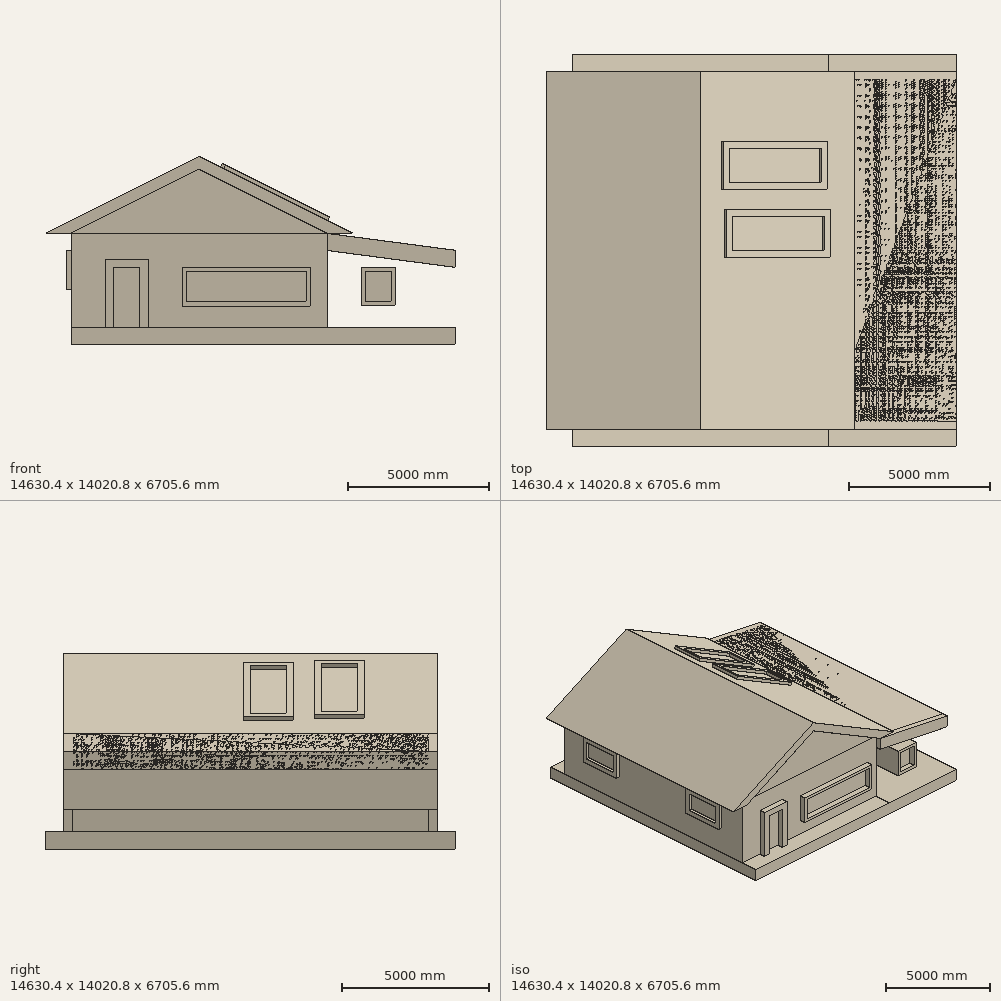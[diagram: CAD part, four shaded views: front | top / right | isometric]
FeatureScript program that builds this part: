
annotation { "Feature Type Name" : "Feature", "Feature Type Description" : "" }
export const myFeature = defineFeature(function(context is Context, id is Id, definition is map)
    precondition{}
    {
        {
            var Q0;
            Q0=qCreatedBy(makeId("Front.planeOp"),FACE);
            var sketch = newSketch(context, id + "F0", { "sketchPlane" : qUnion([Q0])});
            skLineSegment(sketch, "E0", {"start": v(0, 0) * mm, "end": v(4572, 0) * mm});
            skLineSegment(sketch, "E1", {"start": v(0, 0) * mm, "end": v(-4572, 0) * mm});
            skLineSegment(sketch, "E2", {"start": v(0, 0) * mm, "end": v(0, 2286) * mm});
            skLineSegment(sketch, "E3", {"start": v(-4572, 0) * mm, "end": v(0, 2286) * mm});
            skLineSegment(sketch, "E4", {"start": v(0, 2286) * mm, "end": v(4572, 0) * mm});
            skLineSegment(sketch, "E5", {"start": v(-4572, 0) * mm, "end": v(-5486.4, 0) * mm});
            skLineSegment(sketch, "E6", {"start": v(4572, 0) * mm, "end": v(5486.4, 0) * mm});
            skLineSegment(sketch, "E7", {"start": v(0, 2286) * mm, "end": v(0, 2743.2) * mm});
            skLineSegment(sketch, "E8", {"start": v(-5486.4, 0) * mm, "end": v(0, 2743.2) * mm});
            skLineSegment(sketch, "E9", {"start": v(0, 2743.2) * mm, "end": v(5486.4, 0) * mm});
            skLineSegment(sketch, "E10", {"start": v(-4572, 0) * mm, "end": v(-4572, -3352.8) * mm});
            skLineSegment(sketch, "E11", {"start": v(4572, 0) * mm, "end": v(4572, -3352.8) * mm});
            skLineSegment(sketch, "E12", {"start": v(4572, -3352.8) * mm, "end": v(-4572, -3352.8) * mm});
            skLineSegment(sketch, "E13", {"start": v(-4572, -3352.8) * mm, "end": v(-4572, -3962.4) * mm});
            skLineSegment(sketch, "E14", {"start": v(4572, -3352.8) * mm, "end": v(4572, -3962.4) * mm});
            skLineSegment(sketch, "E15", {"start": v(-4572, -3962.4) * mm, "end": v(4572, -3962.4) * mm});
            skLineSegment(sketch, "E16", {"start": v(4572, 0) * mm, "end": v(9144, -603.27) * mm});
            skLineSegment(sketch, "E17", {"start": v(9144, -603.27) * mm, "end": v(9144, -3346.47) * mm});
            skLineSegment(sketch, "E18", {"start": v(9144, -603.27) * mm, "end": v(9144, -1212.87) * mm});
            skLineSegment(sketch, "E19", {"start": v(4572, 0) * mm, "end": v(4572, -609.6) * mm});
            skLineSegment(sketch, "E20", {"start": v(4572, -609.6) * mm, "end": v(9144, -1212.87) * mm});
            skLineSegment(sketch, "E21", {"start": v(4572, -3352.8) * mm, "end": v(9144, -3346.47) * mm});
            skLineSegment(sketch, "E22", {"start": v(4572, -3962.4) * mm, "end": v(9144, -3956.07) * mm});
            skLineSegment(sketch, "E23", {"start": v(9144, -3346.47) * mm, "end": v(9144, -3956.07) * mm});
            skLineSegment(sketch, "E24", {"start": v(-3048, -3352.8) * mm, "end": v(-3048, -1219.2) * mm});
            skLineSegment(sketch, "E25", {"start": v(-3048, -1219.2) * mm, "end": v(-2133.6, -1219.2) * mm});
            skLineSegment(sketch, "E26", {"start": v(-2133.6, -1219.2) * mm, "end": v(-2133.6, -3352.8) * mm});
            skLineSegment(sketch, "E27.0", {"start": v(-1828.8, -914.4) * mm, "end": v(-1828.8, -3352.8) * mm});
            skLineSegment(sketch, "E27.1", {"start": v(-3352.8, -914.4) * mm, "end": v(-1828.8, -914.4) * mm});
            skLineSegment(sketch, "E27.2", {"start": v(-3352.8, -3352.8) * mm, "end": v(-3352.8, -914.4) * mm});
            skLineSegment(sketch, "E28.bottom", {"start": v(-609.6, -1219.2) * mm, "end": v(3962.4, -1219.2) * mm});
            skLineSegment(sketch, "E28.top", {"start": v(-609.6, -2590.8) * mm, "end": v(3962.4, -2590.8) * mm});
            skLineSegment(sketch, "E28.left", {"start": v(-609.6, -1219.2) * mm, "end": v(-609.6, -2590.8) * mm});
            skLineSegment(sketch, "E28.right", {"start": v(3962.4, -1219.2) * mm, "end": v(3962.4, -2590.8) * mm});
            skLineSegment(sketch, "E29.0", {"start": v(-457.2, -1371.6) * mm, "end": v(3810, -1371.6) * mm});
            skLineSegment(sketch, "E29.1", {"start": v(-457.2, -1371.6) * mm, "end": v(-457.2, -2438.4) * mm});
            skLineSegment(sketch, "E29.2", {"start": v(-457.2, -2438.4) * mm, "end": v(3810, -2438.4) * mm});
            skLineSegment(sketch, "E29.3", {"start": v(3810, -1371.6) * mm, "end": v(3810, -2438.4) * mm});
            skLineSegment(sketch, "E30.bottom", {"start": v(5791.2, -1217.51) * mm, "end": v(7010.4, -1217.51) * mm});
            skLineSegment(sketch, "E30.top", {"start": v(5791.2, -2589.11) * mm, "end": v(7010.4, -2589.11) * mm});
            skLineSegment(sketch, "E30.left", {"start": v(5791.2, -1217.51) * mm, "end": v(5791.2, -2589.11) * mm});
            skLineSegment(sketch, "E30.right", {"start": v(7010.4, -1217.51) * mm, "end": v(7010.4, -2589.11) * mm});
            skLineSegment(sketch, "E31.0", {"start": v(5943.6, -1369.91) * mm, "end": v(6858, -1369.91) * mm});
            skLineSegment(sketch, "E31.1", {"start": v(5943.6, -1369.91) * mm, "end": v(5943.6, -2436.71) * mm});
            skLineSegment(sketch, "E31.2", {"start": v(5943.6, -2436.71) * mm, "end": v(6858, -2436.71) * mm});
            skLineSegment(sketch, "E31.3", {"start": v(6858, -1369.91) * mm, "end": v(6858, -2436.71) * mm});
            skSolve(sketch);
        }
        {
            var Q0;
            Q0=makeQuery(id+"F0.imprint","IMPRINT",FACE,{"disambiguationData":[TD([[makeQuery(id+"F0.imprint","IMPRINT",EDGE,{"derivedFrom":sQuery(id+"F0.wireOp",EDGE,"E0")}),-1.0]])]});
            var Q1;
            {var subQ0=sQuery(id+"F0.wireOp",EDGE,"E24");Q1=makeQuery(id+"F0.imprint","IMPRINT",FACE,{"disambiguationData":[TD([[makeQuery(id+"F0.imprint","IMPRINT",EDGE,{"derivedFrom":subQ0}),-1.0]])]});}
            var Q2;
            Q2=makeQuery(id+"F0.imprint","IMPRINT",FACE,{"disambiguationData":[TD([[makeQuery(id+"F0.imprint","IMPRINT",EDGE,{"derivedFrom":sQuery(id+"F0.wireOp",EDGE,"E29.3")}),-1.0]])]});
            var Q3;
            Q3=makeQuery(id+"F0.imprint","IMPRINT",FACE,{"disambiguationData":[TD([[makeQuery(id+"F0.imprint","IMPRINT",EDGE,{"derivedFrom":sQuery(id+"F0.wireOp",EDGE,"E31.0")}),-1.0]])]});
            var Q4;
            Q4=makeQuery(id+"F0.imprint","IMPRINT",FACE,{"disambiguationData":[TD([[makeQuery(id+"F0.imprint","IMPRINT",EDGE,{"derivedFrom":sQuery(id+"F0.wireOp",EDGE,"E11")}),1.0]])]});
            extrude(context, id + "F1", {"entities" : qUnion([Q0, Q1, Q2, Q3, Q4]), "depth" : 6096 * mm, "offsetDistance" : 30.48 * mm, "hasSecondDirection" : true, "secondDirectionOppositeDirection" : true, "secondDirectionDepth" : 6096 * mm});
        }
        {
            var Q0;
            Q0=makeQuery(id+"F0.imprint","IMPRINT",FACE,{"disambiguationData":[TD([[makeQuery(id+"F0.imprint","IMPRINT",EDGE,{"derivedFrom":sQuery(id+"F0.wireOp",EDGE,"E3")}),1.0]])]});
            var Q1;
            Q1=makeQuery(id+"F0.imprint","IMPRINT",FACE,{"disambiguationData":[TD([[makeQuery(id+"F0.imprint","IMPRINT",EDGE,{"derivedFrom":sQuery(id+"F0.wireOp",EDGE,"E16")}),-1.0]])]});
            var Q2;
            Q2=makeQuery(id+"F0.imprint","IMPRINT",FACE,{"disambiguationData":[TD([[makeQuery(id+"F0.imprint","IMPRINT",EDGE,{"derivedFrom":sQuery(id+"F0.wireOp",EDGE,"E4")}),1.0]])]});
            extrude(context, id + "F2", {"entities" : qUnion([Q0, Q1, Q2]), "depth" : 6400.8 * mm, "offsetDistance" : 30.48 * mm, "hasSecondDirection" : true, "secondDirectionOppositeDirection" : true, "secondDirectionDepth" : 6400.8 * mm});
        }
        {
            var Q0;
            {var subQ0=sQuery(id+"F0.wireOp",EDGE,"E24");Q0=makeQuery(id+"F0.imprint","IMPRINT",FACE,{"disambiguationData":[TD([[makeQuery(id+"F0.imprint","IMPRINT",EDGE,{"derivedFrom":subQ0}),1.0]])]});}
            var Q1;
            Q1=makeQuery(id+"F0.imprint","IMPRINT",FACE,{"disambiguationData":[TD([[makeQuery(id+"F0.imprint","IMPRINT",EDGE,{"derivedFrom":sQuery(id+"F0.wireOp",EDGE,"E28.bottom")}),-1.0]])]});
            var Q2;
            Q2=makeQuery(id+"F0.imprint","IMPRINT",FACE,{"disambiguationData":[TD([[makeQuery(id+"F0.imprint","IMPRINT",EDGE,{"derivedFrom":sQuery(id+"F0.wireOp",EDGE,"E30.bottom")}),-1.0]])]});
            extrude(context, id + "F3", {"entities" : qUnion([Q0, Q1, Q2]), "depth" : 6400.8 * mm, "offsetDistance" : 30.48 * mm, "hasSecondDirection" : true, "secondDirectionOppositeDirection" : true, "secondDirectionDepth" : 6400.8 * mm});
        }
        {
            var Q0;
            Q0=makeQuery(id+"F0.imprint","IMPRINT",FACE,{"disambiguationData":[TD([[makeQuery(id+"F0.imprint","IMPRINT",EDGE,{"derivedFrom":sQuery(id+"F0.wireOp",EDGE,"E1")}),-1.0]])]});
            var Q1;
            Q1=makeQuery(id+"F0.imprint","IMPRINT",FACE,{"disambiguationData":[TD([[makeQuery(id+"F0.imprint","IMPRINT",EDGE,{"derivedFrom":sQuery(id+"F0.wireOp",EDGE,"E0")}),1.0]])]});
            extrude(context, id + "F4", {"entities" : qUnion([Q0, Q1]), "depth" : 6096 * mm, "offsetDistance" : 30.48 * mm, "hasSecondDirection" : true, "secondDirectionOppositeDirection" : true, "secondDirectionDepth" : 6096 * mm});
        }
        {
            var Q0;
            {var subQ6=sQuery(id+"F0.wireOp",EDGE,"E13");Q0=makeQuery(id+"F0.imprint","IMPRINT",FACE,{"disambiguationData":[TD([[makeQuery(id+"F0.imprint","IMPRINT",EDGE,{"derivedFrom":subQ6}),1.0]])]});}
            var Q1;
            Q1=makeQuery(id+"F0.imprint","IMPRINT",FACE,{"disambiguationData":[TD([[makeQuery(id+"F0.imprint","IMPRINT",EDGE,{"derivedFrom":sQuery(id+"F0.wireOp",EDGE,"E14")}),1.0]])]});
            extrude(context, id + "F5", {"entities" : qUnion([Q0, Q1]), "depth" : 7010.4 * mm, "offsetDistance" : 30.48 * mm, "hasSecondDirection" : true, "secondDirectionOppositeDirection" : true, "secondDirectionDepth" : 7010.4 * mm});
        }
        {
            var Q0;
            Q0=makeQuery(id+"F1.opExtrude","SWEPT_FACE",FACE,{"disambiguationData":[OSD([sQuery(id+"F0.wireOp",EDGE,"E10")])]});
            var sketch = newSketch(context, id + "F6", { "sketchPlane" : qUnion([Q0])});
            skLineSegment(sketch, "E32.bottom", {"start": v(-4419.6, -853.44) * mm, "end": v(-2590.8, -853.44) * mm});
            skLineSegment(sketch, "E32.top", {"start": v(-4419.6, -1767.84) * mm, "end": v(-2590.8, -1767.84) * mm});
            skLineSegment(sketch, "E32.left", {"start": v(-4419.6, -853.44) * mm, "end": v(-4419.6, -1767.84) * mm});
            skLineSegment(sketch, "E32.right", {"start": v(-2590.8, -853.44) * mm, "end": v(-2590.8, -1767.84) * mm});
            skLineSegment(sketch, "E33.bottom", {"start": v(2590.8, -1767.84) * mm, "end": v(4419.6, -1767.84) * mm});
            skLineSegment(sketch, "E33.top", {"start": v(2590.8, -853.44) * mm, "end": v(4419.6, -853.44) * mm});
            skLineSegment(sketch, "E33.left", {"start": v(2590.8, -1767.84) * mm, "end": v(2590.8, -853.44) * mm});
            skLineSegment(sketch, "E33.right", {"start": v(4419.6, -1767.84) * mm, "end": v(4419.6, -853.44) * mm});
            skLineSegment(sketch, "E34.0", {"start": v(-4663.44, -609.6) * mm, "end": v(-2346.96, -609.6) * mm});
            skLineSegment(sketch, "E34.1", {"start": v(-4663.44, -609.6) * mm, "end": v(-4663.44, -2011.68) * mm});
            skLineSegment(sketch, "E34.2", {"start": v(-4663.44, -2011.68) * mm, "end": v(-2346.96, -2011.68) * mm});
            skLineSegment(sketch, "E34.3", {"start": v(-2346.96, -609.6) * mm, "end": v(-2346.96, -2011.68) * mm});
            skLineSegment(sketch, "E35.0", {"start": v(2346.96, -609.6) * mm, "end": v(4663.44, -609.6) * mm});
            skLineSegment(sketch, "E35.1", {"start": v(2346.96, -2011.68) * mm, "end": v(2346.96, -609.6) * mm});
            skLineSegment(sketch, "E35.2", {"start": v(2346.96, -2011.68) * mm, "end": v(4663.44, -2011.68) * mm});
            skLineSegment(sketch, "E35.3", {"start": v(4663.44, -2011.68) * mm, "end": v(4663.44, -609.6) * mm});
            skSolve(sketch);
        }
        {
            var Q0;
            Q0=makeQuery(id+"F6.imprint","IMPRINT",FACE,{"disambiguationData":[TD([[makeQuery(id+"F6.imprint","IMPRINT",EDGE,{"derivedFrom":sQuery(id+"F6.wireOp",EDGE,"E33.bottom")}),-1.0]])]});
            var Q1;
            Q1=makeQuery(id+"F6.imprint","IMPRINT",FACE,{"disambiguationData":[TD([[makeQuery(id+"F6.imprint","IMPRINT",EDGE,{"derivedFrom":sQuery(id+"F6.wireOp",EDGE,"E32.bottom")}),1.0]])]});
            extrude(context, id + "F7", {"entities" : qUnion([Q0, Q1]), "operationType" : NewBodyOperationType.ADD, "depth" : 152.4 * mm, "offsetDistance" : 30.48 * mm});
        }
        {
            var Q0;
            Q0=makeQuery(id+"F2.opExtrude","SWEPT_FACE",FACE,{"disambiguationData":[OSD([sQuery(id+"F0.wireOp",EDGE,"E9")])]});
            var sketch = newSketch(context, id + "F8", { "sketchPlane" : qUnion([Q0])});
            skLineSegment(sketch, "E36.bottom", {"start": v(-122.01, 3657.6) * mm, "end": v(3535.59, 3657.6) * mm});
            skLineSegment(sketch, "E36.top", {"start": v(-122.01, 2438.4) * mm, "end": v(3535.59, 2438.4) * mm});
            skLineSegment(sketch, "E36.left", {"start": v(-122.01, 3657.6) * mm, "end": v(-122.01, 2438.4) * mm});
            skLineSegment(sketch, "E36.right", {"start": v(3535.59, 3657.6) * mm, "end": v(3535.59, 2438.4) * mm});
            skLineSegment(sketch, "E37.bottom", {"start": v(0, 1219.2) * mm, "end": v(3657.6, 1219.2) * mm});
            skLineSegment(sketch, "E37.top", {"start": v(0, 0) * mm, "end": v(3657.6, 0) * mm});
            skLineSegment(sketch, "E37.left", {"start": v(0, 1219.2) * mm, "end": v(0, 0) * mm});
            skLineSegment(sketch, "E37.right", {"start": v(3657.6, 1219.2) * mm, "end": v(3657.6, 0) * mm});
            skLineSegment(sketch, "E38.0", {"start": v(-243.84, 1463.04) * mm, "end": v(3901.44, 1463.04) * mm});
            skLineSegment(sketch, "E38.1", {"start": v(-243.84, 1463.04) * mm, "end": v(-243.84, -243.84) * mm});
            skLineSegment(sketch, "E38.2", {"start": v(-243.84, -243.84) * mm, "end": v(3901.44, -243.84) * mm});
            skLineSegment(sketch, "E38.3", {"start": v(3901.44, 1463.04) * mm, "end": v(3901.44, -243.84) * mm});
            skLineSegment(sketch, "E39.0", {"start": v(-365.85, 3901.44) * mm, "end": v(3779.43, 3901.44) * mm});
            skLineSegment(sketch, "E39.1", {"start": v(-365.85, 3901.44) * mm, "end": v(-365.85, 2194.56) * mm});
            skLineSegment(sketch, "E39.2", {"start": v(-365.85, 2194.56) * mm, "end": v(3779.43, 2194.56) * mm});
            skLineSegment(sketch, "E39.3", {"start": v(3779.43, 3901.44) * mm, "end": v(3779.43, 2194.56) * mm});
            skSolve(sketch);
        }
        {
            var Q0;
            Q0=makeQuery(id+"F8.imprint","IMPRINT",FACE,{"disambiguationData":[TD([[makeQuery(id+"F8.imprint","IMPRINT",EDGE,{"derivedFrom":sQuery(id+"F8.wireOp",EDGE,"E37.bottom")}),1.0]])]});
            extrude(context, id + "F9", {"entities" : qUnion([Q0]), "operationType" : NewBodyOperationType.ADD, "depth" : 152.4 * mm, "offsetDistance" : 30.48 * mm});
        }
        {
            var Q0;
            Q0=makeQuery(id+"F8.imprint","IMPRINT",FACE,{"disambiguationData":[TD([[makeQuery(id+"F8.imprint","IMPRINT",EDGE,{"derivedFrom":sQuery(id+"F8.wireOp",EDGE,"E36.bottom")}),1.0]])]});
            extrude(context, id + "F10", {"entities" : qUnion([Q0]), "operationType" : NewBodyOperationType.ADD, "depth" : 152.4 * mm, "offsetDistance" : 30.48 * mm});
        }
    });
